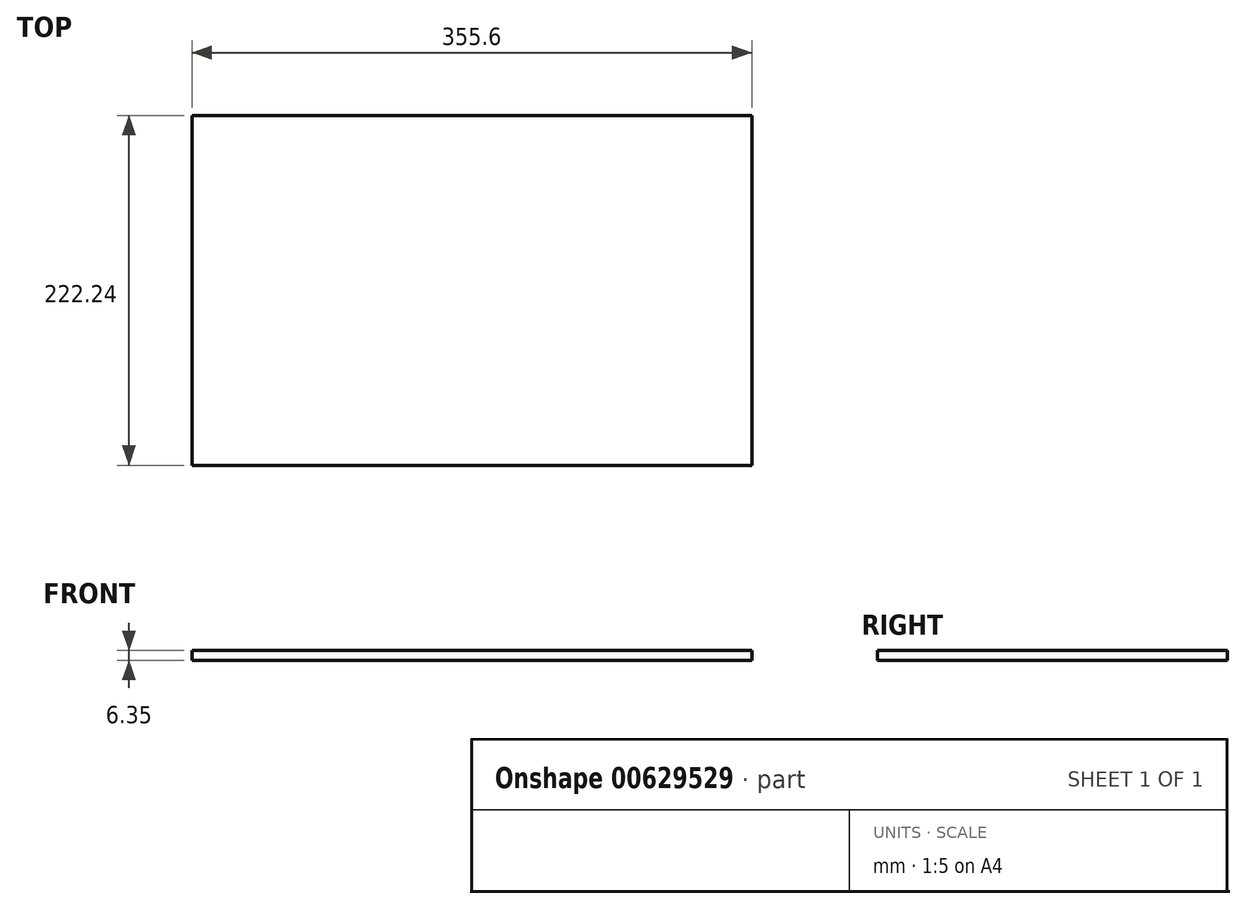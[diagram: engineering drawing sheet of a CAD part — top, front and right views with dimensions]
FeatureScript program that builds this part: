
annotation { "Feature Type Name" : "Feature", "Feature Type Description" : "" }
export const myFeature = defineFeature(function(context is Context, id is Id, definition is map)
    precondition{}
    {
        {
            var Q0;
            Q0=qCreatedBy(makeId("Top.planeOp"),FACE);
            var sketch = newSketch(context, id + "F0", { "sketchPlane" : qUnion([Q0])});
            skLineSegment(sketch, "E0.bottom", {"start": v(-177.8, 111.12) * mm, "end": v(177.8, 111.12) * mm});
            skLineSegment(sketch, "E0.top", {"start": v(-177.8, -111.13) * mm, "end": v(177.8, -111.12) * mm});
            skLineSegment(sketch, "E0.left", {"start": v(-177.8, 111.12) * mm, "end": v(-177.8, -111.13) * mm});
            skLineSegment(sketch, "E0.right", {"start": v(177.8, 111.12) * mm, "end": v(177.8, -111.12) * mm});
            skSolve(sketch);
        }
        {
            var Q0;
            Q0 = qSketchRegion(id + "F0", true);
            extrude(context, id + "F1", {"entities" : qUnion([Q0]), "depth" : 6.35 * mm, "offsetDistance" : 25.4 * mm});
        }
    });
